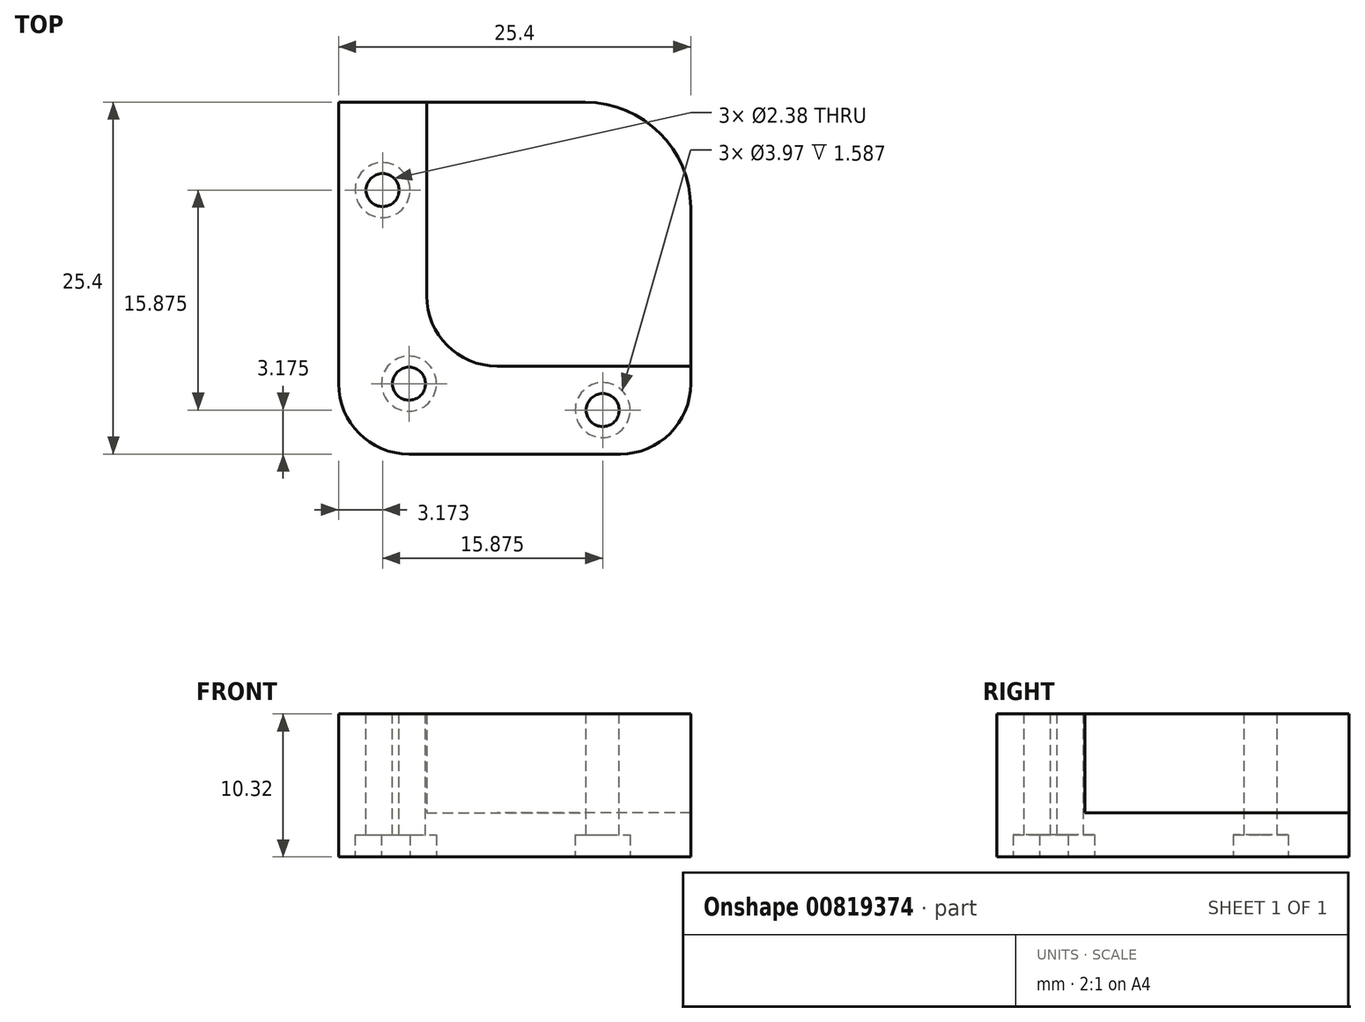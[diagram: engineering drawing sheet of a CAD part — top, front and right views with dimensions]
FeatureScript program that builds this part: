
annotation { "Feature Type Name" : "Feature", "Feature Type Description" : "" }
export const myFeature = defineFeature(function(context is Context, id is Id, definition is map)
    precondition{}
    {
        {
            var Q0;
            Q0=qCreatedBy(makeId("Top.planeOp"),FACE);
            var sketch = newSketch(context, id + "F0", { "sketchPlane" : qUnion([Q0])});
            skLineSegment(sketch, "E0.bottom", {"start": v(2.15, 0) * mm, "end": v(27.55, 0) * mm});
            skLineSegment(sketch, "E0.top", {"start": v(2.15, 25.4) * mm, "end": v(27.55, 25.4) * mm});
            skLineSegment(sketch, "E0.left", {"start": v(2.15, 0) * mm, "end": v(2.15, 25.4) * mm});
            skLineSegment(sketch, "E0.right", {"start": v(27.55, 0) * mm, "end": v(27.55, 25.4) * mm});
            skSolve(sketch);
        }
        {
            var Q0;
            Q0=makeQuery(id+"F0.imprint","IMPRINT",FACE,{"disambiguationData":[TD([[makeQuery(id+"F0.imprint","IMPRINT",EDGE,{"derivedFrom":sQuery(id+"F0.wireOp",EDGE,"E0.bottom")}),1.0]])]});
            extrude(context, id + "F1", {"entities" : qUnion([Q0]), "depth" : 3.17 * mm, "offsetDistance" : 25.4 * mm});
        }
        {
            var Q0;
            Q0=qCreatedBy(makeId("Top.planeOp"),FACE);
            var sketch = newSketch(context, id + "F2", { "sketchPlane" : qUnion([Q0])});
            skLineSegment(sketch, "E1.bottom", {"start": v(2.15, 0) * mm, "end": v(8.5, 0) * mm});
            skLineSegment(sketch, "E1.top", {"start": v(2.15, 25.4) * mm, "end": v(8.5, 25.4) * mm});
            skLineSegment(sketch, "E1.left", {"start": v(2.15, 0) * mm, "end": v(2.15, 25.4) * mm});
            skLineSegment(sketch, "E1.right", {"start": v(8.5, 6.35) * mm, "end": v(8.5, 25.4) * mm});
            skLineSegment(sketch, "E2.bottom", {"start": v(2.15, 0) * mm, "end": v(27.55, 0) * mm});
            skLineSegment(sketch, "E2.top", {"start": v(8.5, 6.35) * mm, "end": v(27.55, 6.35) * mm});
            skLineSegment(sketch, "E2.left", {"start": v(2.15, 0) * mm, "end": v(2.15, 6.35) * mm});
            skLineSegment(sketch, "E2.right", {"start": v(27.55, 0) * mm, "end": v(27.55, 6.35) * mm});
            skSolve(sketch);
        }
        {
            var Q0;
            Q0 = qSketchRegion(id + "F2", true);
            extrude(context, id + "F3", {"entities" : qUnion([Q0]), "operationType" : NewBodyOperationType.ADD, "depth" : 10.32 * mm, "offsetDistance" : 25.4 * mm});
        }
        {
            var Q0;
            Q0=makeQuery(id+"F3.opExtrude","SWEPT_EDGE",EDGE,{"disambiguationData":[OSD([sQuery(id+"F2.wireOp",EDGE,"E1.right"),sQuery(id+"F2.wireOp",EDGE,"E2.top")])]});
            var Q1;
            Q1=makeQuery(id+"F3.boolean.opBoolean","MERGE",EDGE,{"derivedFrom":[makeQuery(id+"F1.opExtrude","SWEPT_EDGE",EDGE,{"disambiguationData":[OSD([sQuery(id+"F0.wireOp",EDGE,"E0.bottom"),sQuery(id+"F0.wireOp",EDGE,"E0.left")])]}),makeQuery(id+"F3.opExtrude","SWEPT_EDGE",EDGE,{"disambiguationData":[OSD([sQuery(id+"F2.wireOp",EDGE,"E2.bottom"),sQuery(id+"F2.wireOp",EDGE,"E2.left")])]})]});
            fillet(context, id + "F4", {"entities" : qUnion([Q0, Q1]), "radius" : 5.08 * mm, "tangentPropagation" : true, "allowEdgeOverflow" : false});
        }
        {
            var Q0;
            Q0=makeQuery(id+"F1.opExtrude","SWEPT_EDGE",EDGE,{"disambiguationData":[OSD([sQuery(id+"F0.wireOp",EDGE,"E0.top"),sQuery(id+"F0.wireOp",EDGE,"E0.right")])]});
            fillet(context, id + "F5", {"entities" : qUnion([Q0]), "radius" : 7.62 * mm, "tangentPropagation" : true, "allowEdgeOverflow" : false});
        }
        {
            var Q0;
            Q0=makeQuery(id+"F3.opExtrude","CAP_FACE",FACE,{"disambiguationData":[OSD([sQuery(id+"F2.wireOp",EDGE,"E1.top"),sQuery(id+"F2.wireOp",EDGE,"E1.left"),sQuery(id+"F2.wireOp",EDGE,"E1.right"),sQuery(id+"F2.wireOp",EDGE,"E2.bottom"),sQuery(id+"F2.wireOp",EDGE,"E2.top"),sQuery(id+"F2.wireOp",EDGE,"E2.left"),sQuery(id+"F2.wireOp",EDGE,"E2.right")])],"isStart":false});
            var sketch = newSketch(context, id + "F6", { "sketchPlane" : qUnion([Q0])});
            skCircle(sketch, "E3", {"center": v(5.32, 19.05) * mm, "radius": 1.2 * mm});
            skCircle(sketch, "E4", {"center": v(7.23, 5.08) * mm, "radius": 1.2 * mm});
            skCircle(sketch, "E5", {"center": v(21.2, 3.17) * mm, "radius": 1.2 * mm});
            skSolve(sketch);
        }
        {
            var Q0;
            Q0=makeQuery(id+"F6.imprint","IMPRINT",FACE,{"disambiguationData":[TD([[makeQuery(id+"F6.imprint","IMPRINT",EDGE,{"derivedFrom":sQuery(id+"F6.wireOp",EDGE,"E4")}),1.0]])]});
            var Q1;
            Q1=makeQuery(id+"F6.imprint","IMPRINT",FACE,{"disambiguationData":[TD([[makeQuery(id+"F6.imprint","IMPRINT",EDGE,{"derivedFrom":sQuery(id+"F6.wireOp",EDGE,"E3")}),1.0]])]});
            var Q2;
            Q2=makeQuery(id+"F6.imprint","IMPRINT",FACE,{"disambiguationData":[TD([[makeQuery(id+"F6.imprint","IMPRINT",EDGE,{"derivedFrom":sQuery(id+"F6.wireOp",EDGE,"E5")}),1.0]])]});
            extrude(context, id + "F7", {"entities" : qUnion([Q0, Q1, Q2]), "operationType" : NewBodyOperationType.REMOVE, "endBound" : BoundingType.THROUGH_ALL, "oppositeDirection" : true, "depth" : 25.4 * mm, "offsetDistance" : 25.4 * mm});
        }
        {
            var Q0;
            Q0=makeQuery(id+"F1.opExtrude","CAP_FACE",FACE,{"disambiguationData":[OSD([sQuery(id+"F0.wireOp",EDGE,"E0.bottom"),sQuery(id+"F0.wireOp",EDGE,"E0.top"),sQuery(id+"F0.wireOp",EDGE,"E0.left"),sQuery(id+"F0.wireOp",EDGE,"E0.right")])],"isStart":true});
            var sketch = newSketch(context, id + "F8", { "sketchPlane" : qUnion([Q0])});
            skCircle(sketch, "E6", {"center": v(7.23, -5.08) * mm, "radius": 1.98 * mm});
            skCircle(sketch, "E7", {"center": v(21.2, -3.17) * mm, "radius": 1.98 * mm});
            skCircle(sketch, "E8", {"center": v(5.32, -19.05) * mm, "radius": 1.98 * mm});
            skSolve(sketch);
        }
        {
            var Q0;
            Q0 = qSketchRegion(id + "F8", true);
            extrude(context, id + "F9", {"entities" : qUnion([Q0]), "operationType" : NewBodyOperationType.REMOVE, "oppositeDirection" : true, "depth" : 1.59 * mm, "offsetDistance" : 25.4 * mm});
        }
    });
